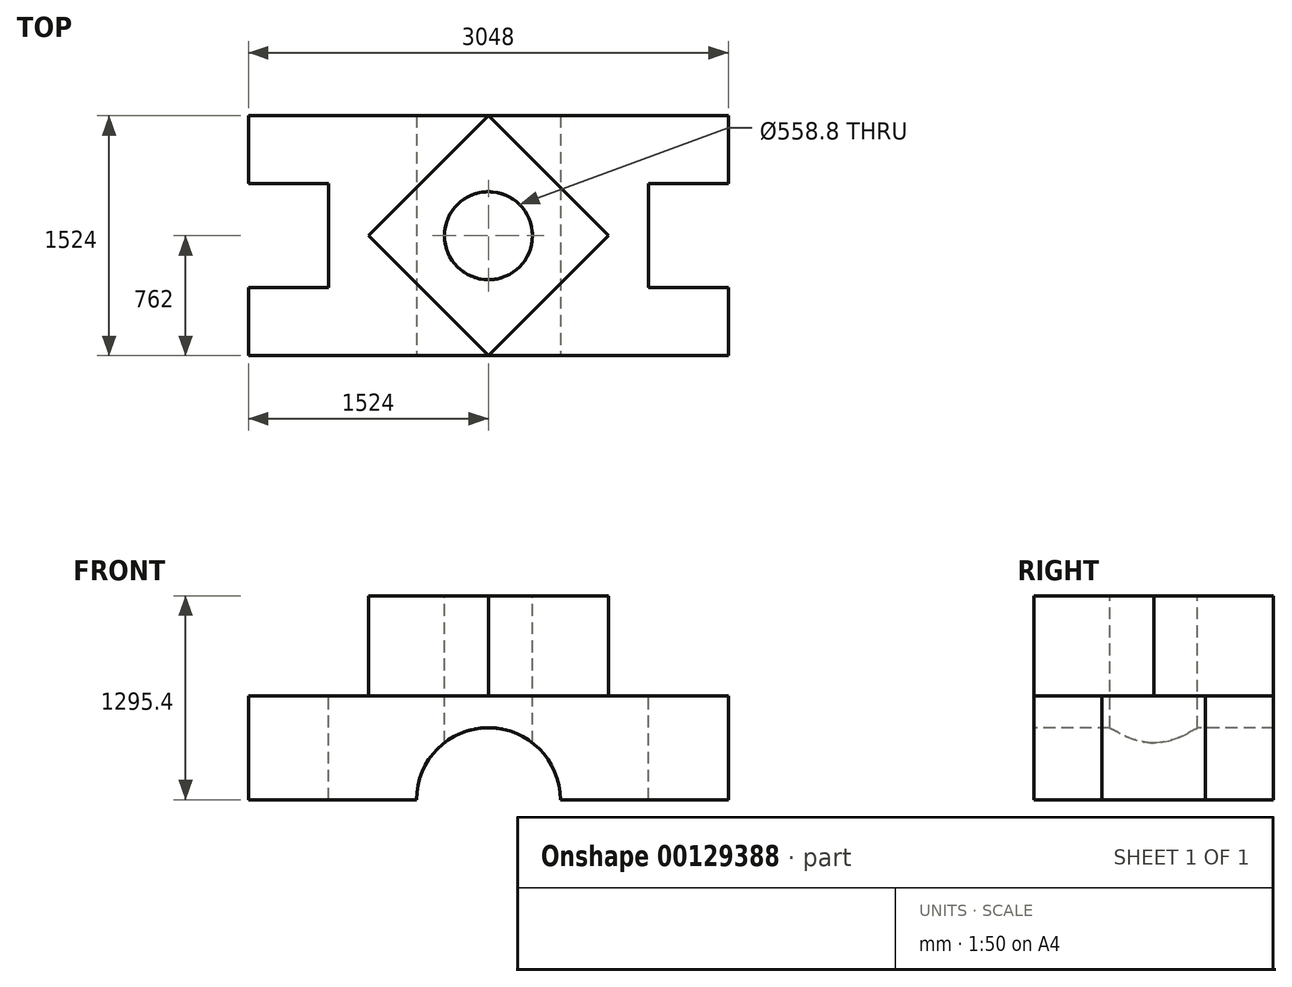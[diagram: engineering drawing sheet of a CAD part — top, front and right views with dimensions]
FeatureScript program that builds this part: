
annotation { "Feature Type Name" : "Feature", "Feature Type Description" : "" }
export const myFeature = defineFeature(function(context is Context, id is Id, definition is map)
    precondition{}
    {
        {
            var Q0;
            Q0=qCreatedBy(makeId("Top.planeOp"),FACE);
            var sketch = newSketch(context, id + "F0", { "sketchPlane" : qUnion([Q0])});
            skLineSegment(sketch, "E0.bottom", {"start": v(1524, -762) * mm, "end": v(-1524, -762) * mm});
            skLineSegment(sketch, "E0.top", {"start": v(1524, 762) * mm, "end": v(-1524, 762) * mm});
            skLineSegment(sketch, "E0.left", {"start": v(1524, -762) * mm, "end": v(1524, 762) * mm});
            skLineSegment(sketch, "E0.right", {"start": v(-1524, -762) * mm, "end": v(-1524, 762) * mm});
            skPoint(sketch, "E0.middle", {"position": v(0, 0) * mm});
            skSolve(sketch);
        }
        {
            var Q0;
            Q0 = qSketchRegion(id + "F0", true);
            extrude(context, id + "F1", {"entities" : qUnion([Q0]), "depth" : 635 * mm});
        }
        {
            var Q0;
            Q0=makeQuery(id+"F1.opExtrude","CAP_FACE",FACE,{"disambiguationData":[OSD([sQuery(id+"F0.wireOp",EDGE,"E0.bottom"),sQuery(id+"F0.wireOp",EDGE,"E0.top"),sQuery(id+"F0.wireOp",EDGE,"E0.left"),sQuery(id+"F0.wireOp",EDGE,"E0.right")])],"isStart":false});
            var sketch = newSketch(context, id + "F2", { "sketchPlane" : qUnion([Q0])});
            skLineSegment(sketch, "E1.bottom", {"start": v(-1016, -330.2) * mm, "end": v(-2032, -330.2) * mm});
            skLineSegment(sketch, "E1.top", {"start": v(-1016, 330.2) * mm, "end": v(-2032, 330.2) * mm});
            skLineSegment(sketch, "E1.left", {"start": v(-1016, -330.2) * mm, "end": v(-1016, 330.2) * mm});
            skLineSegment(sketch, "E1.right", {"start": v(-2032, -330.2) * mm, "end": v(-2032, 330.2) * mm});
            skPoint(sketch, "E1.middle", {"position": v(-1524, 0) * mm});
            skSolve(sketch);
        }
        {
            var Q0;
            Q0 = qSketchRegion(id + "F2", true);
            extrude(context, id + "F3", {"entities" : qUnion([Q0]), "operationType" : NewBodyOperationType.REMOVE, "endBound" : BoundingType.THROUGH_ALL, "oppositeDirection" : true, "depth" : 25.4 * mm});
        }
        {
            var Q0;
            Q0=makeQuery(id+"F1.opExtrude","CAP_FACE",FACE,{"disambiguationData":[OSD([sQuery(id+"F0.wireOp",EDGE,"E0.bottom"),sQuery(id+"F0.wireOp",EDGE,"E0.top"),sQuery(id+"F0.wireOp",EDGE,"E0.left"),sQuery(id+"F0.wireOp",EDGE,"E0.right")])],"isStart":false});
            var sketch = newSketch(context, id + "F4", { "sketchPlane" : qUnion([Q0])});
            skLineSegment(sketch, "E2.bottom", {"start": v(1016, -330.2) * mm, "end": v(2032, -330.2) * mm});
            skLineSegment(sketch, "E2.top", {"start": v(1016, 330.2) * mm, "end": v(2032, 330.2) * mm});
            skLineSegment(sketch, "E2.left", {"start": v(1016, -330.2) * mm, "end": v(1016, 330.2) * mm});
            skLineSegment(sketch, "E2.right", {"start": v(2032, -330.2) * mm, "end": v(2032, 330.2) * mm});
            skPoint(sketch, "E2.middle", {"position": v(1524, 0) * mm});
            skSolve(sketch);
        }
        {
            var Q0;
            Q0 = qSketchRegion(id + "F4", true);
            extrude(context, id + "F5", {"entities" : qUnion([Q0]), "operationType" : NewBodyOperationType.REMOVE, "endBound" : BoundingType.THROUGH_ALL, "oppositeDirection" : true, "depth" : 25.4 * mm});
        }
        {
            var Q0;
            Q0=makeQuery(id+"F1.opExtrude","CAP_FACE",FACE,{"disambiguationData":[OSD([sQuery(id+"F0.wireOp",EDGE,"E0.bottom"),sQuery(id+"F0.wireOp",EDGE,"E0.top"),sQuery(id+"F0.wireOp",EDGE,"E0.left"),sQuery(id+"F0.wireOp",EDGE,"E0.right")])],"isStart":false});
            extrude(context, id + "F6", {"entities" : qUnion([Q0]), "operationType" : NewBodyOperationType.ADD, "depth" : 25.4 * mm});
        }
        {
            var Q0;
            Q0=makeQuery(id+"F6.opExtrude","CAP_FACE",FACE,{"disambiguationData":[OSD([sQuery(id+"F0.wireOp",EDGE,"E0.bottom"),sQuery(id+"F0.wireOp",EDGE,"E0.top"),sQuery(id+"F0.wireOp",EDGE,"E0.left"),sQuery(id+"F0.wireOp",EDGE,"E0.right")])],"isStart":false});
            var sketch = newSketch(context, id + "F7", { "sketchPlane" : qUnion([Q0])});
            skLineSegment(sketch, "E3", {"start": v(0, 762) * mm, "end": v(-762, 0) * mm});
            skLineSegment(sketch, "E4", {"start": v(-762, 0) * mm, "end": v(0, -762) * mm});
            skLineSegment(sketch, "E5", {"start": v(0, -762) * mm, "end": v(762, 0) * mm});
            skLineSegment(sketch, "E6", {"start": v(762, 0) * mm, "end": v(0, 762) * mm});
            skSolve(sketch);
        }
        {
            var Q0;
            Q0 = qSketchRegion(id + "F7", true);
            extrude(context, id + "F8", {"entities" : qUnion([Q0]), "operationType" : NewBodyOperationType.ADD, "depth" : 635 * mm});
        }
        {
            var Q0;
            Q0=makeQuery(id+"F8.opExtrude","CAP_FACE",FACE,{"disambiguationData":[OSD([sQuery(id+"F7.wireOp",EDGE,"E3"),sQuery(id+"F7.wireOp",EDGE,"E4"),sQuery(id+"F7.wireOp",EDGE,"E5"),sQuery(id+"F7.wireOp",EDGE,"E6")])],"isStart":false});
            var sketch = newSketch(context, id + "F9", { "sketchPlane" : qUnion([Q0])});
            skCircle(sketch, "E7", {"center": v(0, 0) * mm, "radius": 279.4 * mm});
            skSolve(sketch);
        }
        {
            var Q0;
            Q0 = qSketchRegion(id + "F9", true);
            extrude(context, id + "F10", {"entities" : qUnion([Q0]), "operationType" : NewBodyOperationType.REMOVE, "endBound" : BoundingType.THROUGH_ALL, "oppositeDirection" : true, "depth" : 25.4 * mm});
        }
        {
            var Q0;
            {var subQ0=sQuery(id+"F0.wireOp",EDGE,"E0.bottom");Q0=makeQuery(id+"F6.boolean.opBoolean","MERGE",FACE,{"derivedFrom":[makeQuery(id+"F1.opExtrude","SWEPT_FACE",FACE,{"disambiguationData":[OSD([subQ0])]}),makeQuery(id+"F6.opExtrude","SWEPT_FACE",FACE,{"disambiguationData":[OSD([subQ0])]})]});}
            var sketch = newSketch(context, id + "F11", { "sketchPlane" : qUnion([Q0])});
            skCircle(sketch, "E8", {"center": v(0, 0) * mm, "radius": 457.2 * mm});
            skSolve(sketch);
        }
        {
            var Q0;
            Q0 = qSketchRegion(id + "F11", true);
            extrude(context, id + "F12", {"entities" : qUnion([Q0]), "operationType" : NewBodyOperationType.REMOVE, "endBound" : BoundingType.THROUGH_ALL, "oppositeDirection" : true, "depth" : 25.4 * mm});
        }
    });
